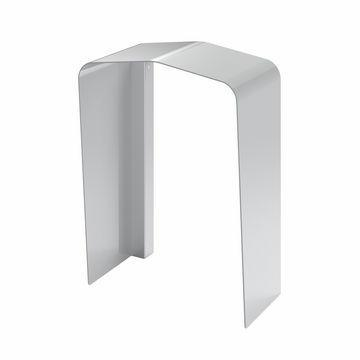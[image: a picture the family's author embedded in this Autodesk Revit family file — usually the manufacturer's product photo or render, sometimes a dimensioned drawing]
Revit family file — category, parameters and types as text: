
# Revit family: Building-ElectricalVehicleCharging-GEWISS-JOINON-ICON_PROTECTION-COVER
name_source: partatom
category: Apparecchi elettrici
units: mm (PartAtom-declared; Revit-internal decimal feet)

## family parameters
Condiviso = No
Host = Superficie
Mantenere orientamento annotazione = Sì
Punto di calcolo locali = Sì
Quota connettore circolare = Usa diametro
Taglio con vuoti quando caricato = No
Tipo di parte = Normale

## types (1)
- GWJ8104 - I-CON - PROTECTION COVER
    BLOCCO = B=C
    Catalogue = E-MOBILITY
    Description: = I-CON protection cover
    Descrizione = I-CON - PROTECTION COVER
    EAN code = 8034035071393
    Electrocod = 2242
    FORMULA = 1000 mm  [stored 3.28084 ft]
    IDF = 9caf37bf-1025-4629-8f26-cf455c1d0b63
    IDT = de4cf1b2-9fd5-41ee-a883-306328bc9e16
    Immagine tipo = ICON_TETTUCCIO.jpg
    L = 155 mm  [stored 0.50853 ft]
    Modello = GWJ8104
    N.poli = 1
    POMELLO = bianco
    PRESA = Giallo
    Produttore = GEWISS S.p.A.
    Prospetto di default = 1219 mm
    STRUTTURA = RAL - 7035
    STRUTTURA ALTA = blue
    Spostamento_S = 1500 mm  [stored 4.92126 ft]
    Suitable for = WallBox I-CON
    Technical sheet = https://www.gewiss.com
    URL = https://www.gewiss.com
    VETRO = Vetro
    Version file RFA = 19.4
    Voltaggio = 0 V
    W = 115 mm  [stored 0.377297 ft]

note: [stored X ft] marks values corroborated as IEEE doubles in the binary element streams (Revit-internal decimal feet)
